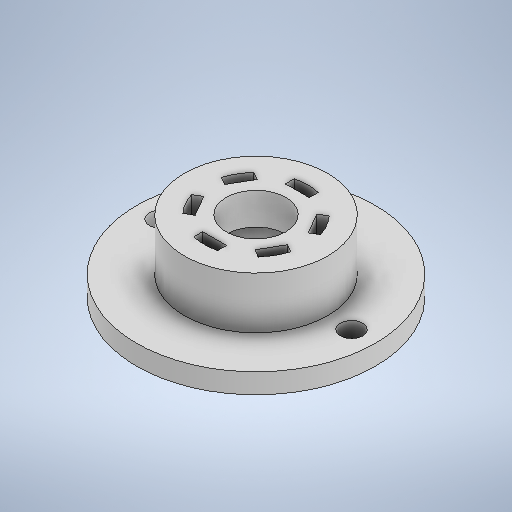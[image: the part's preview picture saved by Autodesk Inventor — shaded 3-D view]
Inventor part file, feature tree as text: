
AUTODESK INVENTOR PART (.ipt)
format: ipt  version: 2025 (Build 290162000, 162)  size: 321,536 bytes
history: native  units: in
note: dims shown in document units (in); Inventor stores cm internally (conversion verified against a paired STEP export)
features: sketch x5, extrude x4, projected_geometry x3
ambient origin geometry x8: Origin, YZ Plane, XZ Plane, XY Plane, X Axis, Y Axis, Z Axis, Center Point
bodies: Solid1 (feature_tree)
feature tree (12):
  sketch  "Sketch1"  dims[d0=0.2953in d1=0.5118in]
  extrude  "Extrusion1"  Depth=0.5118in
  extrude  "Extrusion2"  Depth=0.1575in TaperAngle=0.0deg
  extrude  "Extrusion3"  Depth=0.1969in
  extrude  "Extrusion4"  Depth=0.2047in
  sketch  "Sketch2"  dims[d5=0.1969in d6=0.0in d7=0.0591in]
  projected_geometry  "Projected Loop1"
  projected_geometry  "Projected Loop2"
  sketch  "Sketch Circular Pattern1"  dims[d2=0.0984in d3=0.1575in d4=0.0in]
  sketch  "Sketch3"  dims[d10=2.3622in d12=360.0deg d14=0.1575in d15=0.0in d16=1.1811in d17=0.0984in d18=0.0in d19=0.1102in d20=0.4724in d21=0.7874in d23=360.0deg]
  projected_geometry  "Projected Loop3"
  sketch  "Sketch Circular Pattern2"  dims[d8=0.0512in d9=0.2047in]
